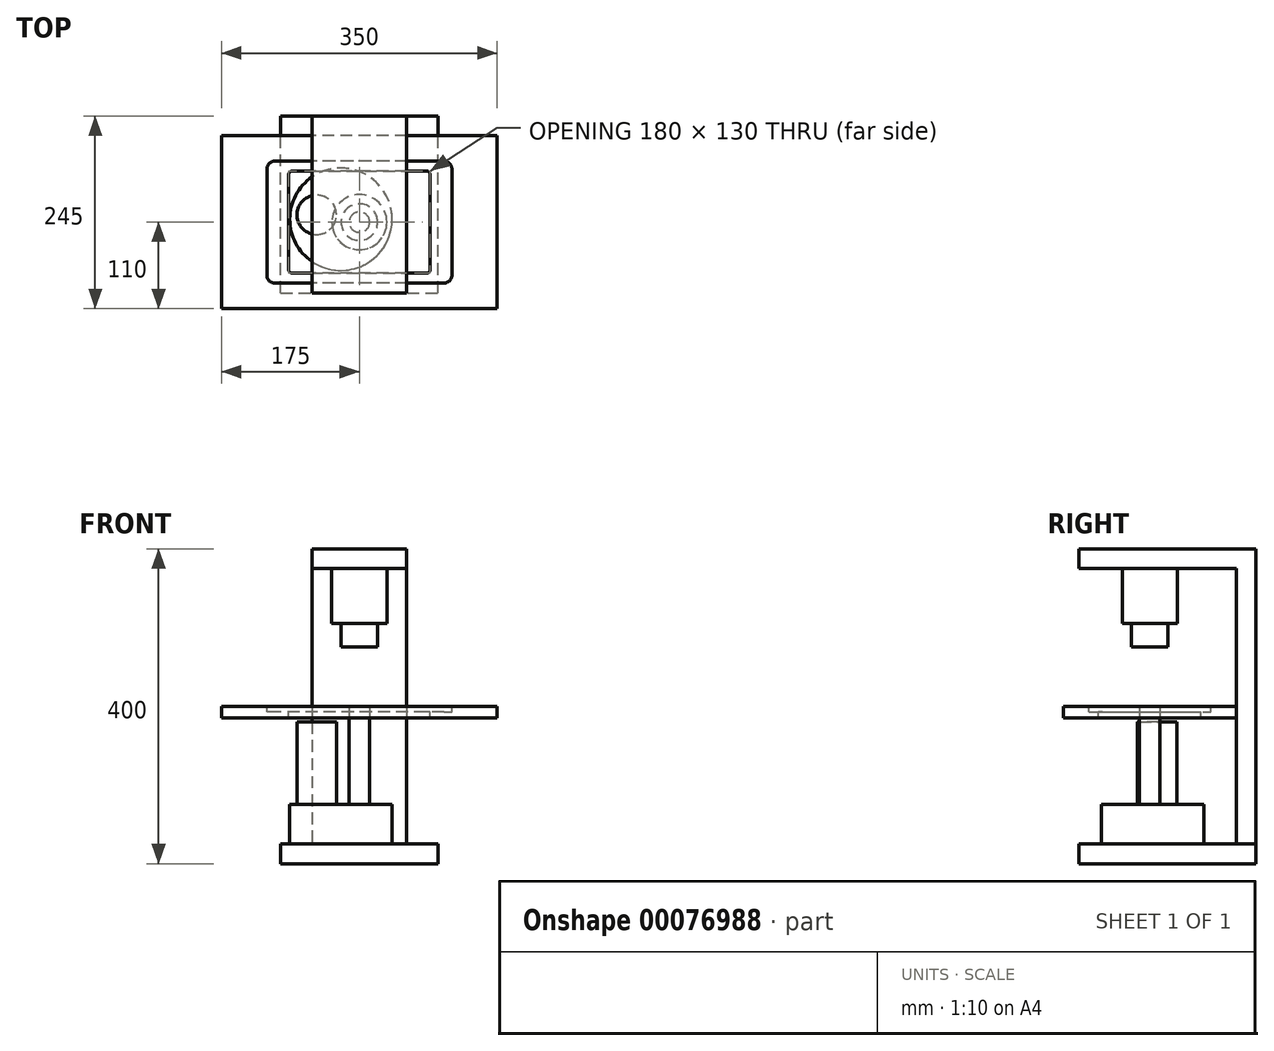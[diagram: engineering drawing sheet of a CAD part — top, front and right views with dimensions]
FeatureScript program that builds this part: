
annotation { "Feature Type Name" : "Feature", "Feature Type Description" : "" }
export const myFeature = defineFeature(function(context is Context, id is Id, definition is map)
    precondition{}
    {
        {
            var Q0;
            Q0=qCreatedBy(makeId("Front.planeOp"),FACE);
            var sketch = newSketch(context, id + "F0", { "sketchPlane" : qUnion([Q0])});
            skLineSegment(sketch, "E0.rect.bottom", {"start": v(60, 200) * mm, "end": v(-60, 200) * mm});
            skLineSegment(sketch, "E0.rect.top", {"start": v(60, -200) * mm, "end": v(-60, -200) * mm});
            skLineSegment(sketch, "E0.rect.left", {"start": v(60, 200) * mm, "end": v(60, -200) * mm});
            skLineSegment(sketch, "E0.rect.right", {"start": v(-60, 200) * mm, "end": v(-60, -200) * mm});
            skPoint(sketch, "E0.rect.middle", {"position": v(0, 0) * mm});
            skSolve(sketch);
        }
        {
            var Q0;
            Q0=makeQuery(id+"F0.imprint","IMPRINT",FACE,{"disambiguationData":[TD([[makeQuery(id+"F0.imprint","IMPRINT",EDGE,{"derivedFrom":sQuery(id+"F0.wireOp",EDGE,"E0.rect.bottom")}),1.0]])]});
            extrude(context, id + "F1", {"entities" : qUnion([Q0]), "depth" : 25 * mm});
        }
        {
            var Q0;
            Q0=makeQuery(id+"F1.opExtrude","CAP_FACE",FACE,{"disambiguationData":[OSD([sQuery(id+"F0.wireOp",EDGE,"E0.rect.bottom"),sQuery(id+"F0.wireOp",EDGE,"E0.rect.top"),sQuery(id+"F0.wireOp",EDGE,"E0.rect.left"),sQuery(id+"F0.wireOp",EDGE,"E0.rect.right")])],"isStart":false});
            var sketch = newSketch(context, id + "F2", { "sketchPlane" : qUnion([Q0])});
            skLineSegment(sketch, "E1.bottom", {"start": v(-60, 200) * mm, "end": v(60, 200) * mm});
            skLineSegment(sketch, "E1.top", {"start": v(-60, 175) * mm, "end": v(60, 175) * mm});
            skLineSegment(sketch, "E1.left", {"start": v(-60, 200) * mm, "end": v(-60, 175) * mm});
            skLineSegment(sketch, "E1.right", {"start": v(60, 200) * mm, "end": v(60, 175) * mm});
            skSolve(sketch);
        }
        {
            var Q0;
            Q0=makeQuery(id+"F2.imprint","IMPRINT",FACE,{"disambiguationData":[TD([[makeQuery(id+"F2.imprint","IMPRINT",EDGE,{"derivedFrom":sQuery(id+"F2.wireOp",EDGE,"E1.bottom")}),1.0]])]});
            extrude(context, id + "F3", {"entities" : qUnion([Q0]), "operationType" : NewBodyOperationType.ADD, "depth" : 200 * mm});
        }
        {
            var Q0;
            Q0=makeQuery(id+"F3.opExtrude","SWEPT_FACE",FACE,{"disambiguationData":[OSD([sQuery(id+"F2.wireOp",EDGE,"E1.top")])]});
            var sketch = newSketch(context, id + "F4", { "sketchPlane" : qUnion([Q0])});
            skLineSegment(sketch, "E2", {"start": v(0, 25) * mm, "end": v(0, 135) * mm, "construction": true});
            skPoint(sketch, "E2.endSnap0", {"position": v(0, 25) * mm});
            skCircle(sketch, "E3", {"center": v(0, 135) * mm, "radius": 35 * mm});
            skSolve(sketch);
        }
        {
            var Q0;
            Q0=makeQuery(id+"F4.imprint","IMPRINT",FACE,{"disambiguationData":[TD([[makeQuery(id+"F4.imprint","IMPRINT",EDGE,{"derivedFrom":sQuery(id+"F4.wireOp",EDGE,"E3")}),1.0]])]});
            extrude(context, id + "F5", {"entities" : qUnion([Q0]), "operationType" : NewBodyOperationType.ADD, "depth" : 70 * mm});
        }
        {
            var Q0;
            Q0=makeQuery(id+"F5.opExtrude","CAP_FACE",FACE,{"disambiguationData":[OSD([sQuery(id+"F4.wireOp",EDGE,"E3")])],"isStart":false});
            var sketch = newSketch(context, id + "F6", { "sketchPlane" : qUnion([Q0])});
            skCircle(sketch, "E4", {"center": v(0, 135) * mm, "radius": 23.2 * mm});
            skSolve(sketch);
        }
        {
            var Q0;
            Q0=makeQuery(id+"F6.imprint","IMPRINT",FACE,{"disambiguationData":[TD([[makeQuery(id+"F6.imprint","IMPRINT",EDGE,{"derivedFrom":sQuery(id+"F6.wireOp",EDGE,"E4")}),1.0]])]});
            extrude(context, id + "F7", {"entities" : qUnion([Q0]), "operationType" : NewBodyOperationType.ADD, "depth" : 30 * mm});
        }
        {
            var Q0;
            Q0=makeQuery(id+"F1.opExtrude","CAP_FACE",FACE,{"disambiguationData":[OSD([sQuery(id+"F0.wireOp",EDGE,"E0.rect.bottom"),sQuery(id+"F0.wireOp",EDGE,"E0.rect.top"),sQuery(id+"F0.wireOp",EDGE,"E0.rect.left"),sQuery(id+"F0.wireOp",EDGE,"E0.rect.right")])],"isStart":false});
            var sketch = newSketch(context, id + "F8", { "sketchPlane" : qUnion([Q0])});
            skLineSegment(sketch, "E5.bottom", {"start": v(-100, -200) * mm, "end": v(100, -200) * mm});
            skLineSegment(sketch, "E5.top", {"start": v(-100, -175) * mm, "end": v(100, -175) * mm});
            skLineSegment(sketch, "E5.left", {"start": v(-100, -200) * mm, "end": v(-100, -175) * mm});
            skLineSegment(sketch, "E5.right", {"start": v(100, -200) * mm, "end": v(100, -175) * mm});
            skSolve(sketch);
        }
        {
            var Q0;
            {var subQ3=sQuery(id+"F8.wireOp",EDGE,"E5.left");Q0=makeQuery(id+"F8.imprint","IMPRINT",FACE,{"disambiguationData":[TD([[makeQuery(id+"F8.imprint","IMPRINT",EDGE,{"derivedFrom":subQ3}),-1.0]])]});}
            var Q1;
            {var subQ0=sQuery(id+"F8.wireOp",EDGE,"E5.bottom");var subQ1=makeQuery(id+"F1.opExtrude","CAP_EDGE",EDGE,{"disambiguationData":[OSD([sQuery(id+"F0.wireOp",EDGE,"E0.rect.left")])],"isStart":false});var subQ2=makeQuery(id+"F8.imprint","INTERSECT",VERTEX,{"derivedFrom":[subQ1,subQ0]});var subQ3=makeQuery(id+"F1.opExtrude","CAP_EDGE",EDGE,{"disambiguationData":[OSD([sQuery(id+"F0.wireOp",EDGE,"E0.rect.right")])],"isStart":false});var subQ4=makeQuery(id+"F8.imprint","INTERSECT",VERTEX,{"derivedFrom":[subQ3,subQ0]});Q1=makeQuery(id+"F8.imprint","IMPRINT",FACE,{"disambiguationData":[TD([[makeQuery(id+"F8.imprint","IMPRINT",EDGE,{"disambiguationData":[TD([[subQ2,-1.0],[subQ4,1.0]])],"derivedFrom":subQ0}),-1.0]])]});}
            var Q2;
            {var subQ3=sQuery(id+"F8.wireOp",EDGE,"E5.right");Q2=makeQuery(id+"F8.imprint","IMPRINT",FACE,{"disambiguationData":[TD([[makeQuery(id+"F8.imprint","IMPRINT",EDGE,{"derivedFrom":subQ3}),1.0]])]});}
            extrude(context, id + "F9", {"entities" : qUnion([Q0, Q1, Q2]), "operationType" : NewBodyOperationType.ADD, "depth" : 200 * mm, "hasSecondDirection" : true, "secondDirectionOppositeDirection" : true, "secondDirectionDepth" : 25 * mm});
        }
        {
            var Q0;
            Q0=makeQuery(id+"F9.opExtrude","SWEPT_FACE",FACE,{"disambiguationData":[OSD([sQuery(id+"F8.wireOp",EDGE,"E5.top")])]});
            var sketch = newSketch(context, id + "F10", { "sketchPlane" : qUnion([Q0])});
            skCircle(sketch, "E6", {"center": v(-23.46, -131.4) * mm, "radius": 65 * mm});
            skSolve(sketch);
        }
        {
            var Q0;
            Q0=makeQuery(id+"F10.imprint","IMPRINT",FACE,{"disambiguationData":[TD([[makeQuery(id+"F10.imprint","IMPRINT",EDGE,{"derivedFrom":sQuery(id+"F10.wireOp",EDGE,"E6")}),1.0]])]});
            extrude(context, id + "F11", {"entities" : qUnion([Q0]), "operationType" : NewBodyOperationType.ADD, "depth" : 50 * mm});
        }
        {
            var Q0;
            Q0=makeQuery(id+"F11.opExtrude","CAP_FACE",FACE,{"disambiguationData":[OSD([sQuery(id+"F10.wireOp",EDGE,"E6")])],"isStart":false});
            var sketch = newSketch(context, id + "F12", { "sketchPlane" : qUnion([Q0])});
            skCircle(sketch, "E7", {"center": v(0, -135) * mm, "radius": 13 * mm});
            skSolve(sketch);
        }
        {
            var Q0;
            Q0=makeQuery(id+"F12.imprint","IMPRINT",FACE,{"disambiguationData":[TD([[makeQuery(id+"F12.imprint","IMPRINT",EDGE,{"derivedFrom":sQuery(id+"F12.wireOp",EDGE,"E7")}),1.0]])]});
            extrude(context, id + "F13", {"entities" : qUnion([Q0]), "operationType" : NewBodyOperationType.ADD, "depth" : 125 * mm});
        }
        {
            var Q0;
            Q0=makeQuery(id+"F11.opExtrude","CAP_FACE",FACE,{"disambiguationData":[OSD([sQuery(id+"F10.wireOp",EDGE,"E6")])],"isStart":false});
            var sketch = newSketch(context, id + "F14", { "sketchPlane" : qUnion([Q0])});
            skCircle(sketch, "E8", {"center": v(-54.21, -125.71) * mm, "radius": 25 * mm});
            skSolve(sketch);
        }
        {
            var Q0;
            Q0=makeQuery(id+"F14.imprint","IMPRINT",FACE,{"disambiguationData":[TD([[makeQuery(id+"F14.imprint","IMPRINT",EDGE,{"derivedFrom":sQuery(id+"F14.wireOp",EDGE,"E8")}),1.0]])]});
            extrude(context, id + "F15", {"entities" : qUnion([Q0]), "operationType" : NewBodyOperationType.ADD, "depth" : 105 * mm});
        }
        {
            var Q0;
            Q0=qCreatedBy(makeId("Top.planeOp"),FACE);
            var sketch = newSketch(context, id + "F16", { "sketchPlane" : qUnion([Q0])});
            skLineSegment(sketch, "E9.rect.bottom", {"start": v(175, -245) * mm, "end": v(-175, -245) * mm});
            skLineSegment(sketch, "E9.rect.top", {"start": v(175, -25) * mm, "end": v(-175, -25) * mm});
            skLineSegment(sketch, "E9.rect.left", {"start": v(175, -245) * mm, "end": v(175, -25) * mm});
            skLineSegment(sketch, "E9.rect.right", {"start": v(-175, -245) * mm, "end": v(-175, -25) * mm});
            skPoint(sketch, "E9.rect.middle", {"position": v(0, -135) * mm});
            skLineSegment(sketch, "E10.rect.bottom", {"start": v(107.5, -212.5) * mm, "end": v(-107.5, -212.5) * mm});
            skLineSegment(sketch, "E10.rect.top", {"start": v(107.5, -57.5) * mm, "end": v(-107.5, -57.5) * mm});
            skLineSegment(sketch, "E10.rect.left", {"start": v(117.5, -202.5) * mm, "end": v(117.5, -67.5) * mm});
            skLineSegment(sketch, "E10.rect.right", {"start": v(-117.5, -202.5) * mm, "end": v(-117.5, -67.5) * mm});
            skPoint(sketch, "E11.visualSharp", {"position": v(-117.5, -57.5) * mm});
            skArc(sketch, "E11.filletArc", {"start": v(-107.5, -57.5) * mm, "mid": v(-114.57, -60.43) * mm, "end": v(-117.5, -67.5) * mm});
            skPoint(sketch, "E12.visualSharp", {"position": v(-117.5, -212.5) * mm});
            skArc(sketch, "E12.filletArc", {"start": v(-117.5, -202.5) * mm, "mid": v(-114.57, -209.57) * mm, "end": v(-107.5, -212.5) * mm});
            skPoint(sketch, "E13.visualSharp", {"position": v(117.5, -212.5) * mm});
            skArc(sketch, "E13.filletArc", {"start": v(107.5, -212.5) * mm, "mid": v(114.57, -209.57) * mm, "end": v(117.5, -202.5) * mm});
            skPoint(sketch, "E14.visualSharp", {"position": v(117.5, -57.5) * mm});
            skArc(sketch, "E14.filletArc", {"start": v(117.5, -67.5) * mm, "mid": v(114.57, -60.43) * mm, "end": v(107.5, -57.5) * mm});
            skSolve(sketch);
        }
        {
            var Q0;
            Q0=makeQuery(id+"F16.imprint","IMPRINT",FACE,{"disambiguationData":[TD([[makeQuery(id+"F16.imprint","IMPRINT",EDGE,{"derivedFrom":sQuery(id+"F16.wireOp",EDGE,"E9.rect.bottom")}),-1.0]])]});
            extrude(context, id + "F17", {"entities" : qUnion([Q0]), "operationType" : NewBodyOperationType.ADD, "oppositeDirection" : true, "depth" : 15 * mm});
        }
        {
            var Q0;
            Q0=makeQuery(id+"F17.opExtrude","SWEPT_FACE",FACE,{"disambiguationData":[OSD([sQuery(id+"F16.wireOp",EDGE,"E10.rect.top")])]});
            var sketch = newSketch(context, id + "F18", { "sketchPlane" : qUnion([Q0])});
            skLineSegment(sketch, "E15.rect.bottom", {"start": v(117.5, -15) * mm, "end": v(-117.5, -15) * mm});
            skLineSegment(sketch, "E15.rect.top", {"start": v(117.5, -7.5) * mm, "end": v(-117.5, -7.5) * mm});
            skLineSegment(sketch, "E15.rect.left", {"start": v(117.5, -15) * mm, "end": v(117.5, -7.5) * mm});
            skLineSegment(sketch, "E15.rect.right", {"start": v(-117.5, -15) * mm, "end": v(-117.5, -7.5) * mm});
            skPoint(sketch, "E15.rect.middle", {"position": v(0, -11.25) * mm});
            skSolve(sketch);
        }
        {
            var Q0;
            {var subQ0=sQuery(id+"F18.wireOp",EDGE,"E15.rect.bottom");var subQ1=sQuery(id+"F16.wireOp",EDGE,"E10.rect.top");var subQ2=makeQuery(id+"F17.opExtrude","SWEPT_EDGE",EDGE,{"disambiguationData":[OSD([subQ1,sQuery(id+"F16.wireOp",EDGE,"E14.filletArc")])]});var subQ3=makeQuery(id+"F18.imprint","INTERSECT",VERTEX,{"derivedFrom":[subQ2,subQ0]});Q0=makeQuery(id+"F18.imprint","IMPRINT",FACE,{"disambiguationData":[TD([[makeQuery(id+"F18.imprint","IMPRINT",EDGE,{"disambiguationData":[TD([[subQ3,-1.0]])],"derivedFrom":subQ0}),-1.0]])]});}
            var Q1;
            {var subQ3=sQuery(id+"F18.wireOp",EDGE,"E15.rect.right");Q1=makeQuery(id+"F18.imprint","IMPRINT",FACE,{"disambiguationData":[TD([[makeQuery(id+"F18.imprint","IMPRINT",EDGE,{"derivedFrom":subQ3}),-1.0]])]});}
            var Q2;
            {var subQ3=sQuery(id+"F18.wireOp",EDGE,"E15.rect.left");Q2=makeQuery(id+"F18.imprint","IMPRINT",FACE,{"disambiguationData":[TD([[makeQuery(id+"F18.imprint","IMPRINT",EDGE,{"derivedFrom":subQ3}),1.0]])]});}
            extrude(context, id + "F19", {"entities" : qUnion([Q0, Q1, Q2]), "operationType" : NewBodyOperationType.ADD, "depth" : 155 * mm});
        }
        {
            var Q0;
            Q0=makeQuery(id+"F19.opExtrude","SWEPT_FACE",FACE,{"disambiguationData":[OSD([sQuery(id+"F18.wireOp",EDGE,"E15.rect.top")])]});
            var sketch = newSketch(context, id + "F20", { "sketchPlane" : qUnion([Q0])});
            skLineSegment(sketch, "E16.rect.bottom", {"start": v(90, -200) * mm, "end": v(-90, -200) * mm});
            skLineSegment(sketch, "E16.rect.top", {"start": v(90, -70) * mm, "end": v(-90, -70) * mm});
            skLineSegment(sketch, "E16.rect.left", {"start": v(90, -200) * mm, "end": v(90, -70) * mm});
            skLineSegment(sketch, "E16.rect.right", {"start": v(-90, -200) * mm, "end": v(-90, -70) * mm});
            skPoint(sketch, "E16.rect.middle", {"position": v(0, -135) * mm});
            skSolve(sketch);
        }
        {
            var Q0;
            Q0=makeQuery(id+"F20.imprint","IMPRINT",FACE,{"disambiguationData":[TD([[makeQuery(id+"F20.imprint","IMPRINT",EDGE,{"derivedFrom":sQuery(id+"F20.wireOp",EDGE,"E16.rect.bottom")}),-1.0]])]});
            extrude(context, id + "F21", {"entities" : qUnion([Q0]), "operationType" : NewBodyOperationType.REMOVE, "endBound" : BoundingType.UP_TO_NEXT, "oppositeDirection" : true, "depth" : 25 * mm});
        }
        {
            var Q0;
            Q0=makeQuery(id+"F21.boolean.opBoolean","COPY",EDGE,{"derivedFrom":makeQuery(id+"F21.opExtrude","SWEPT_EDGE",EDGE,{"disambiguationData":[OSD([sQuery(id+"F20.wireOp",EDGE,"E16.rect.top"),sQuery(id+"F20.wireOp",EDGE,"E16.rect.right")])]})});
            var Q1;
            Q1=makeQuery(id+"F21.boolean.opBoolean","COPY",EDGE,{"derivedFrom":makeQuery(id+"F21.opExtrude","SWEPT_EDGE",EDGE,{"disambiguationData":[OSD([sQuery(id+"F20.wireOp",EDGE,"E16.rect.top"),sQuery(id+"F20.wireOp",EDGE,"E16.rect.left")])]})});
            var Q2;
            Q2=makeQuery(id+"F21.boolean.opBoolean","COPY",EDGE,{"derivedFrom":makeQuery(id+"F21.opExtrude","SWEPT_EDGE",EDGE,{"disambiguationData":[OSD([sQuery(id+"F20.wireOp",EDGE,"E16.rect.bottom"),sQuery(id+"F20.wireOp",EDGE,"E16.rect.right")])]})});
            var Q3;
            Q3=makeQuery(id+"F21.boolean.opBoolean","COPY",EDGE,{"derivedFrom":makeQuery(id+"F21.opExtrude","SWEPT_EDGE",EDGE,{"disambiguationData":[OSD([sQuery(id+"F20.wireOp",EDGE,"E16.rect.bottom"),sQuery(id+"F20.wireOp",EDGE,"E16.rect.left")])]})});
            fillet(context, id + "F22", {"entities" : qUnion([Q0, Q1, Q2, Q3]), "radius" : 5 * mm, "tangentPropagation" : true, "allowEdgeOverflow" : false});
        }
    });
